FCSTD DOCUMENT  (FreeCAD 0.15R4671 (Git))
Label: layout
License: All rights reserved
LicenseURL: http://en.wikipedia.org/wiki/All_rights_reserved
objects: Sketcher::SketchObject×1
note: 1 computed .brp shape members not serialized (recipe doc carries the construction recipe); baked Part::Feature solids carry a one-line shape summary decoded from their .brp

FEATURE [Sketcher::SketchObject] Sketch  label="WorkLines"
  Placement = pos=(0,0,6.35) rot=(0,0,1;0rad)
  sketch-geometry (13):
    g0: LineSegment [constr] StartX=-63.5 StartY=-46.342 StartZ=0 EndX=63.5 EndY=-46.342 EndZ=0
    g1: LineSegment [constr] StartX=63.5 StartY=-46.342 StartZ=0 EndX=63.5 EndY=-62.217 EndZ=0
    g2: LineSegment [constr] StartX=63.5 StartY=-62.217 StartZ=0 EndX=-63.5 EndY=-62.217 EndZ=0
    g3: LineSegment [constr] StartX=-63.5 StartY=-62.217 StartZ=0 EndX=-63.5 EndY=-46.342 EndZ=0
    g4: Circle [constr] CenterX=0 CenterY=0 CenterZ=0 NormalX=0 NormalY=0 NormalZ=1 Radius=88.9
    g5: Circle [constr] CenterX=0 CenterY=0 CenterZ=0 NormalX=0 NormalY=0 NormalZ=1 Radius=82.55
    g6: Circle CenterX=0 CenterY=0 CenterZ=0 NormalX=0 NormalY=0 NormalZ=1 Radius=11
    g7: Circle CenterX=0 CenterY=0 CenterZ=0 NormalX=0 NormalY=0 NormalZ=1 Radius=22.25
    g8: LineSegment StartX=-21.336 StartY=79.7451 StartZ=0 EndX=21.336 EndY=79.7451 EndZ=0
    g9: LineSegment StartX=21.336 StartY=79.7451 StartZ=0 EndX=21.336 EndY=37.0731 EndZ=0
    g10: LineSegment StartX=21.336 StartY=37.0731 StartZ=0 EndX=-21.336 EndY=37.0731 EndZ=0
    g11: LineSegment StartX=-21.336 StartY=37.0731 StartZ=0 EndX=-21.336 EndY=79.7451 EndZ=0
    g12: Circle CenterX=0 CenterY=0 CenterZ=0 NormalX=0 NormalY=0 NormalZ=1 Radius=72.5
  constraints (34):
    c: Coincident(g0,g1)
    c: Coincident(g1,g2)
    c: Coincident(g2,g3)
    c: Coincident(g3,g0)
    c: Horizontal(g0)
    c: Horizontal(g2)
    c: Vertical(g1)
    c: Vertical(g3)
    c: Symmetric(g0,g0,g-2)
    c: DistanceY(g0,g1) = -15.875
    c: DistanceX(g0,g0) = 127
    c: Coincident(g4,g-1)
    c: Radius(g4) = 88.9
    c: PointOnObject(g2,g4)
    c: Radius(g5) = 82.55
    c: Coincident(g5,g-1)
    c: Coincident(g6,g-1)
    c: Radius(g6) = 11
    c: Coincident(g7,g-1)
    c: Radius(g7) = 22.25
    c: Coincident(g8,g9)
    c: Coincident(g9,g10)
    c: Coincident(g10,g11)
    c: Coincident(g11,g8)
    c: Horizontal(g8)
    c: Horizontal(g10)
    c: Vertical(g9)
    c: Vertical(g11)
    c: DistanceX(g8) = 42.672
    c: Equal(g8,g9)
    c: PointOnObject(g8,g5)
    c: PointOnObject(g8,g5)
    c: Coincident(g12,g-1)
    c: Radius(g12) = 72.5
